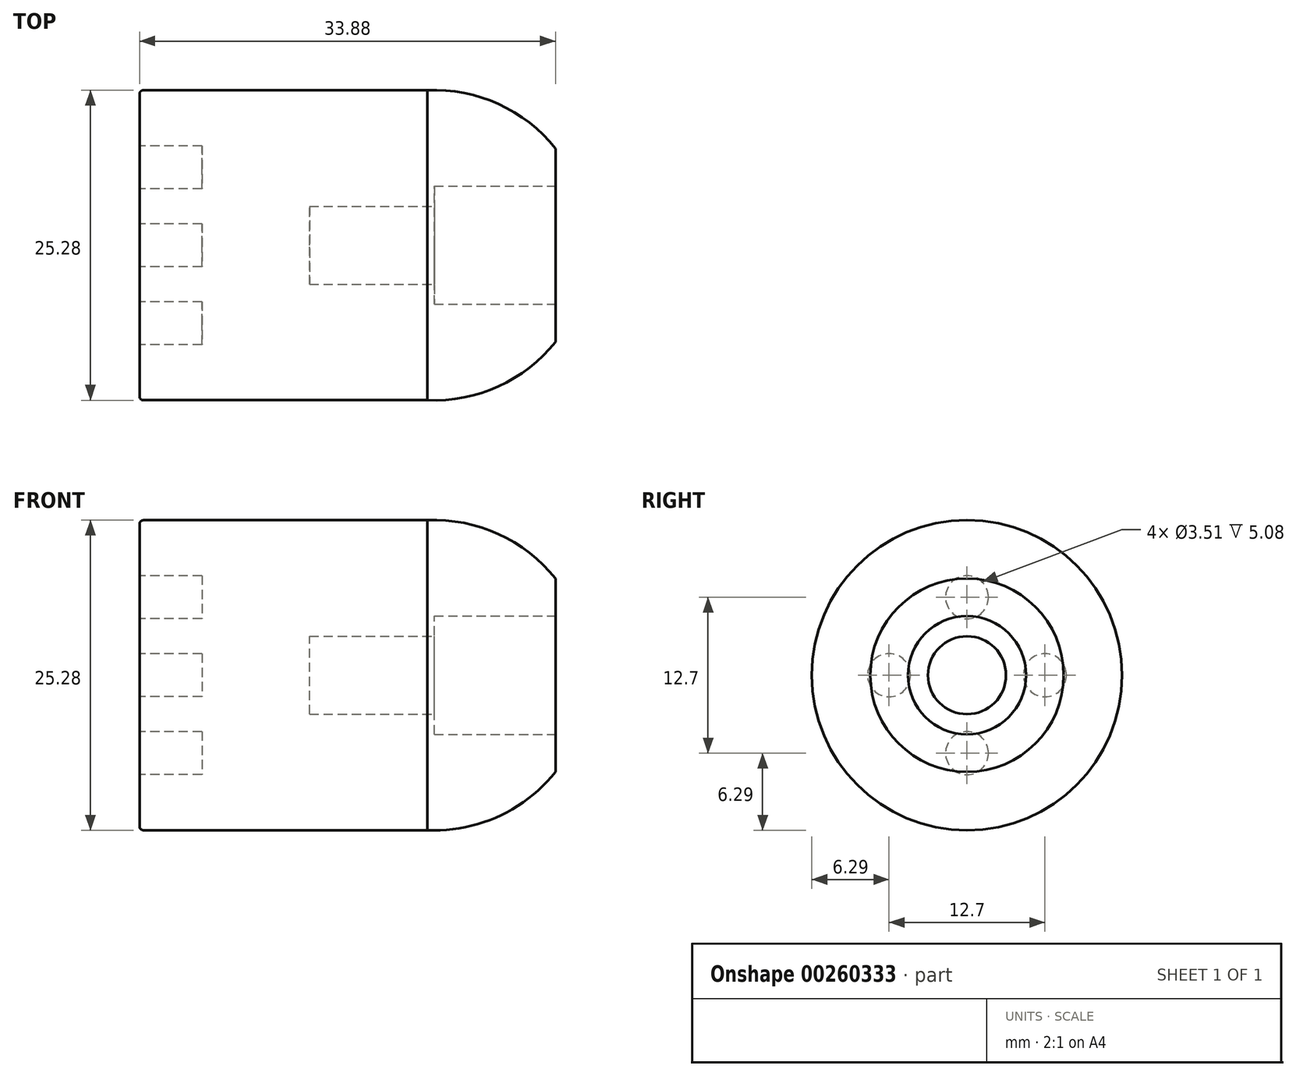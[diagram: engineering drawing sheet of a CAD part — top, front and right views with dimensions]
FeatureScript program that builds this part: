
annotation { "Feature Type Name" : "Feature", "Feature Type Description" : "" }
export const myFeature = defineFeature(function(context is Context, id is Id, definition is map)
    precondition{}
    {
        {
            var Q0;
            Q0=qCreatedBy(makeId("Front.planeOp"),FACE);
            var sketch = newSketch(context, id + "F0", { "sketchPlane" : qUnion([Q0])});
            skLineSegment(sketch, "E0", {"start": v(0, 0) * mm, "end": v(0, 12.62) * mm});
            skLineSegment(sketch, "E1", {"start": v(0, 12.62) * mm, "end": v(24.56, 12.62) * mm});
            skLineSegment(sketch, "E2", {"start": v(33.88, 4.81) * mm, "end": v(24, 4.81) * mm});
            skLineSegment(sketch, "E3", {"start": v(24, 4.81) * mm, "end": v(24, 3.18) * mm});
            skLineSegment(sketch, "E4", {"start": v(24, 3.18) * mm, "end": v(13.84, 3.18) * mm});
            skLineSegment(sketch, "E5", {"start": v(13.84, 3.18) * mm, "end": v(13.84, 0) * mm});
            skLineSegment(sketch, "E6", {"start": v(13.84, 0) * mm, "end": v(0, 0) * mm});
            skPoint(sketch, "E7.orphan", {"position": v(37.13, 0) * mm});
            skPoint(sketch, "E8.end.orphan", {"position": v(24, 2.4) * mm});
            skPoint(sketch, "E9.orphan", {"position": v(24, 0) * mm});
            skLineSegment(sketch, "E10", {"start": v(33.88, 7.88) * mm, "end": v(33.88, 4.81) * mm});
            skLineSegment(sketch, "E11", {"start": v(24.56, 12.62) * mm, "end": v(24.56, 4.81) * mm});
            skArc(sketch, "E12", {"start": v(33.88, 7.88) * mm, "mid": v(29.23, 11.5) * mm, "end": v(23.44, 12.62) * mm});
            skSolve(sketch);
        }
        {
            var Q0;
            Q0=qSketchRegion(id+"F0",true);
            var Q1;
            Q1=sQuery(id+"F0.wireOp",EDGE,"E6");
            revolve(context, id + "F1", {"entities" : qUnion([Q0]), "axis" : qUnion([Q1]), "revolveType" : RevolveType.FULL});
        }
        {
            var Q0;
            Q0=makeQuery(id+"F1.opRevolve","SWEPT_FACE",FACE,{"disambiguationData":[OSD([sQuery(id+"F0.wireOp",EDGE,"E0")])]});
            var sketch = newSketch(context, id + "F2", { "sketchPlane" : qUnion([Q0])});
            skCircle(sketch, "E13", {"center": v(0, 6.35) * mm, "radius": 1.75 * mm});
            skCircle(sketch, "E14", {"center": v(-6.35, 0) * mm, "radius": 1.75 * mm});
            skCircle(sketch, "E15", {"center": v(0, -6.35) * mm, "radius": 1.75 * mm});
            skCircle(sketch, "E16", {"center": v(6.35, 0) * mm, "radius": 1.75 * mm});
            skSolve(sketch);
        }
        {
            var Q0;
            Q0=qSketchRegion(id+"F2",true);
            extrude(context, id + "F3", {"entities" : qUnion([Q0]), "operationType" : NewBodyOperationType.REMOVE, "oppositeDirection" : true, "depth" : 5.08 * mm});
        }
        {
            var Q0;
            Q0=makeQuery(id+"F1.opRevolve","SWEPT_EDGE",EDGE,{"disambiguationData":[OSD([sQuery(id+"F0.wireOp",EDGE,"E0"),sQuery(id+"F0.wireOp",EDGE,"E1")])]});
            fillet(context, id + "F4", {"entities" : qUnion([Q0]), "radius" : 0.3 * mm, "tangentPropagation" : true, "allowEdgeOverflow" : false});
        }
    });
